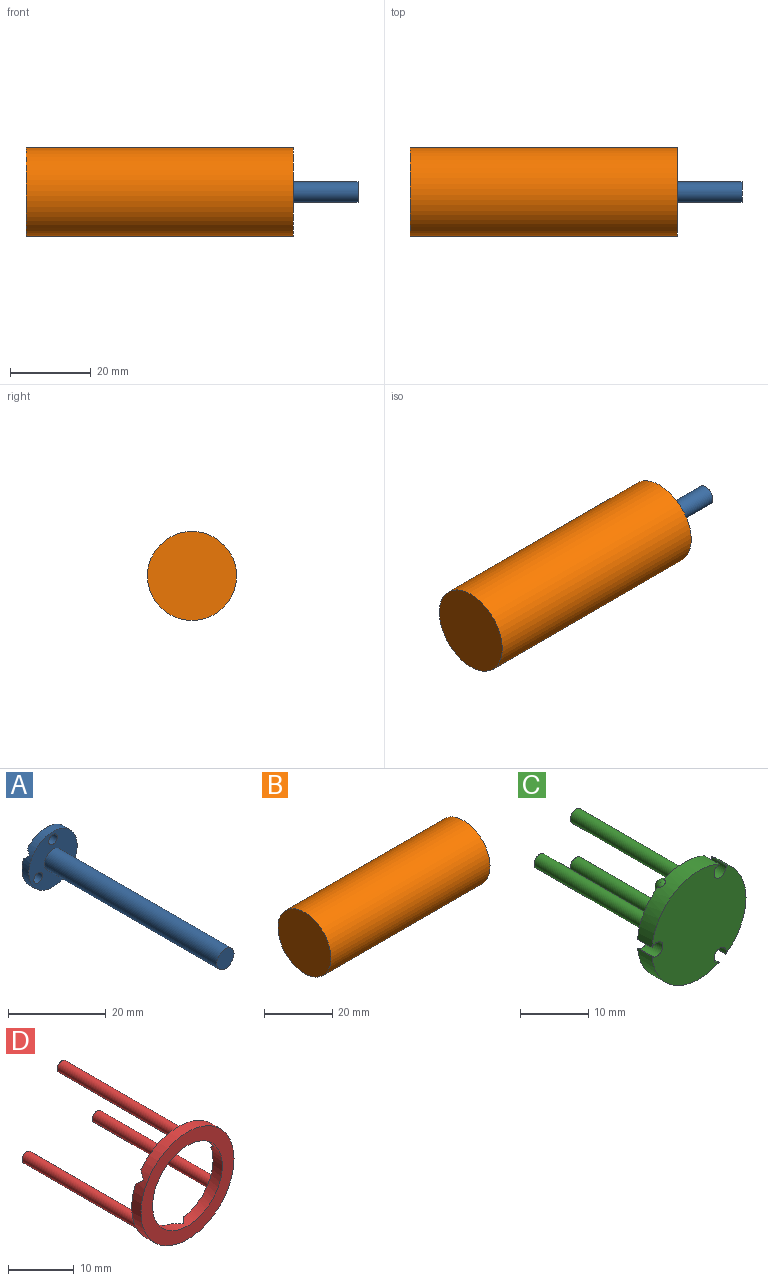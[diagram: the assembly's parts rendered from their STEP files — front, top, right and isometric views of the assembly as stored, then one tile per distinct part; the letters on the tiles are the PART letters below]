
ASSEMBLY  parts=4 mates=2
PART A: 18 faces, bbox 14x52x14 mm
  f0: cylinder r=7mm len=14mm, axis (0,1,0), area 83.6mm2, adj f1,f3,f4,f5,f6,f7,f8,f10
  f1: plane 9.31x5.8mm, normal (0,1,0), area 30.5mm2, adj f0,f3,f11,f12
  f2: cylinder r=1mm len=2mm, axis (0,1,0), area 8mm2, adj f3,f4,f6,f10,f12,f13,f17
  f3: plane 6.5x1.2mm, normal (-0.71,0.71,0), area 10.5mm2, adj f0,f1,f2,f6,f12
  f4: plane 6.07x3.99mm, normal (-0.35,0.71,-0.61), area 10.5mm2, adj f0,f2,f5,f10,f13
  f5: plane 10.75x5.61mm, normal (0,1,0), area 30.5mm2, adj f0,f4,f9,f13
  f6: plane 6.5x1.2mm, normal (0.71,0.71,0), area 10.5mm2, adj f0,f2,f3,f7,f10
  f7: plane 9.31x5.8mm, normal (0,1,0), area 30.5mm2, adj f0,f6,f10,f14
  f8: plane 14x14mm, normal (0,-1,0), area 119.6mm2, adj f0,f9,f11,f14,f16
  f9: cylinder r=1.25mm len=2.5mm, axis (0,1,0), area 15.7mm2, adj f5,f8
  f10: plane 5.71x4.2mm, normal (0.35,0.71,0.61), area 10.5mm2, adj f0,f2,f4,f6,f7
  f11: cylinder r=1.25mm len=2.5mm, axis (0,1,0), area 15.7mm2, adj f1,f8
  f12: plane 5.71x4.2mm, normal (-0.35,0.71,0.61), area 10.5mm2, adj f0,f1,f2,f3,f13
  f13: plane 6.07x3.99mm, normal (0.35,0.71,-0.61), area 10.5mm2, adj f0,f2,f4,f5,f12
  f14: cylinder r=1.25mm len=2.5mm, axis (0,1,0), area 15.7mm2, adj f7,f8
  f15: plane 5x5mm, normal (0,-1,0), area 19.6mm2, adj f16
  f16: cylinder r=2.5mm len=50mm, axis (0,1,0), area 785.4mm2, adj f8,f15
  f17: plane 2x2mm, normal (0,1,0), area 3.1mm2, adj f2
PART B: 11 faces, bbox 66x22x22 mm
  f0: cylinder r=11mm len=66mm, axis (1,0,0), area 4561.6mm2, adj f1,f10
  f1: plane 22x22mm, normal (-1,0,0), area 380.1mm2, adj f0
  f2: plane 20x20mm, normal (1,0,0), area 314.2mm2, adj f3
  f3: cylinder r=10mm len=30mm, axis (1,0,0), area 1885mm2, adj f2,f4
  f4: plane 20x20mm, normal (-1,0,0), area 87.2mm2, adj f3,f5
  f5: cylinder r=8.5mm len=17mm, axis (1,0,0), area 106.8mm2, adj f4,f6
  f6: plane 20x20mm, normal (1,0,0), area 87.2mm2, adj f5,f7
  f7: cylinder r=10mm len=30mm, axis (1,0,0), area 1885mm2, adj f6,f8
  f8: plane 20x20mm, normal (-1,0,0), area 290.4mm2, adj f7,f9
  f9: cylinder r=2.75mm len=5.5mm, axis (1,0,0), area 34.6mm2, adj f8,f10
  f10: plane 22x22mm, normal (1,0,0), area 356.4mm2, adj f0,f9
PART C: 20 faces, bbox 19.7x28x19.5 mm
  f0: cylinder r=9.75mm len=16.04mm, axis (0,1,0), area 55.8mm2, adj f2,f3,f5,f16,f19
  f1: cylinder r=9.75mm len=13.89mm, axis (0,1,0), area 55.8mm2, adj f2,f3,f6,f13,f19
  f2: plane 19.5x19.47mm, normal (0,-1,0), area 284.7mm2, adj f0,f1,f4,f13,f16,f19
  f3: plane 19.5x19.44mm, normal (0,1,0), area 245mm2, adj f0,f1,f4,f5,f6,f7,f8,f9
  f4: cylinder r=9.75mm len=13.89mm, axis (0,1,0), area 55.8mm2, adj f2,f3,f7,f13,f16
  f5: sphere r=1.2mm, area 9.8mm2, adj f0,f3
  f6: sphere r=1.2mm, area 9.8mm2, adj f1,f3
  f7: sphere r=1.2mm, area 9.8mm2, adj f3,f4
  f8: sphere r=1.2mm, area 9mm2, adj f3
  f9: sphere r=1.2mm, area 9mm2, adj f3
  f10: sphere r=1.2mm, area 9mm2, adj f3
  f11: cylinder r=1.18mm len=25mm, axis (0,-1,0), area 185.9mm2, adj f3,f12
  f12: plane 2.37x2.37mm, normal (0,1,0), area 4.4mm2, adj f11
  f13: cylinder r=1.25mm len=3mm, axis (0,1,0), area 18.4mm2, adj f1,f2,f3,f4
  f14: cylinder r=1.18mm len=25mm, axis (0,-1,0), area 185.9mm2, adj f3,f15
  f15: plane 2.37x2.37mm, normal (0,1,0), area 4.4mm2, adj f14
  f16: cylinder r=1.25mm len=3mm, axis (0,1,0), area 18.4mm2, adj f0,f2,f3,f4
  f17: cylinder r=1.18mm len=25mm, axis (0,-1,0), area 185.9mm2, adj f3,f18
  f18: plane 2.37x2.37mm, normal (0,1,0), area 4.4mm2, adj f17
  f19: cylinder r=1.25mm len=3mm, axis (0,1,0), area 18.4mm2, adj f0,f1,f2,f3
PART D: 18 faces, bbox 20x27x20 mm
  f0: cylinder r=7.5mm len=15mm, axis (0,1,0), area 89.9mm2, adj f2,f3,f4,f5,f6,f7,f8,f9
  f1: cylinder r=10mm len=20mm, axis (0,1,0), area 121.3mm2, adj f2,f3,f4,f5,f6,f7,f8,f9
  f2: plane 13.85x8.8mm, normal (0,1,0), area 36.7mm2, adj f0,f1,f6,f11,f14
  f3: plane 16x5.26mm, normal (0,1,0), area 36.7mm2, adj f0,f1,f9,f10,f12
  f4: plane 20x20mm, normal (0,-1,0), area 137.4mm2, adj f0,f1
  f5: plane 13.85x8.8mm, normal (0,1,0), area 36.7mm2, adj f0,f1,f7,f8,f16
  f6: plane 2.6x1.2mm, normal (-0.71,0.71,0), area 4.3mm2, adj f0,f1,f2,f7
  f7: plane 2.6x1.2mm, normal (0.71,0.71,0), area 4.3mm2, adj f0,f1,f5,f6
  f8: plane 2.71x2.34mm, normal (0.35,0.71,0.61), area 4.3mm2, adj f0,f1,f5,f9
  f9: plane 2.85x2.26mm, normal (-0.35,0.71,-0.61), area 4.3mm2, adj f0,f1,f3,f8
  f10: plane 2.85x2.26mm, normal (0.35,0.71,-0.61), area 4.3mm2, adj f0,f1,f3,f11
  f11: plane 2.71x2.34mm, normal (-0.35,0.71,0.61), area 4.3mm2, adj f0,f1,f2,f10
  f12: cylinder r=1mm len=25mm, axis (0,-1,0), area 157.1mm2, adj f3,f13
  f13: plane 2x2mm, normal (0,1,0), area 3.1mm2, adj f12
  f14: cylinder r=1mm len=25mm, axis (0,-1,0), area 157.1mm2, adj f2,f15
  f15: plane 2x2mm, normal (0,1,0), area 3.1mm2, adj f14
  f16: cylinder r=1mm len=25mm, axis (0,-1,0), area 157.1mm2, adj f5,f17
  f17: plane 2x2mm, normal (0,1,0), area 3.1mm2, adj f16
PLACE A rot(axis=(0,0,1),90deg) t=(0.68,-15.68,13.58)mm
PLACE B t=(32.59,-15.68,13.58)mm
PLACE C rot(axis=(-0.25,-0.25,-0.94),93.8deg) t=(0.19,-15.68,13.58)mm
PLACE D rot(axis=(0,0,1),90deg) t=(0.68,-15.68,13.58)mm
MATE cylindrical A.f0 <-> D.f0  axis (-1,0,0) through (1.68,-15.68,13.58)mm
MATE fastened D.f0 <-> B.f0  axis (1,0,0) through (2.68,-15.68,13.58)mm
